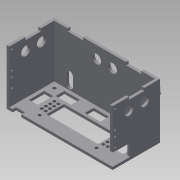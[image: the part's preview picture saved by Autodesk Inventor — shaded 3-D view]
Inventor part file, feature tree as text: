
AUTODESK INVENTOR PART (.ipt)
format: ipt  version: 2015 SP1 (Build 190203100, 203)  size: 1,242,624 bytes
history: native  units: mm
features: extrude x27, sketch x23, projected_geometry x7, fillet x1, plane x1, chamfer x1
ambient origin geometry x8: Origin, YZ Plane, XZ Plane, XY Plane, X Axis, Y Axis, Z Axis, Center Point
bodies: Body1 (feature_tree)
feature tree (60):
  sketch  "Sketch1"  dims[d49=120.812mm d51=3.0mm]
  extrude  "Extrusion5"  Depth=3.0mm
  extrude  "Extrusion6"  Depth=3.0mm TaperAngle=0.0deg
  extrude  "Extrusion7"  Depth=3.0mm
  extrude  "Extrusion8"  Depth=51.214111mm
  extrude  "Extrusion9"  Depth=3.5mm TaperAngle=0.0deg
  extrude  "Extrusion10"  Depth=17.5mm
  sketch  "Sketch12"  dims[d65=10.0mm d66=17.5mm]
  extrude  "Extrusion11"  Depth=10.0mm TaperAngle=0.0deg
  extrude  "Extrusion12"  Depth=3.0mm TaperAngle=0.0deg
  fillet  "Fillet2"  Radius=22.0mm
  extrude  "Extrusion13"  Depth=15.0mm
  plane  "Work Plane1"
  sketch  "Sketch20"  dims[d80=3.0mm d81=0.0mm d82=10.0mm d83=0.0mm d84=22.0mm]
  extrude  "Extrusion26"  Depth=200.0mm TaperAngle=0.0deg
  sketch  "Sketch25"  dims[d87=10.0mm d88=200.0mm d89=0.0mm]
  extrude  "Extrusion28"  Depth=2.0mm
  extrude  "Extrusion29"  Depth=3.5mm
  extrude  "Extrusion30"  Depth=3.5mm
  chamfer  "Chamfer1"  Distance=10.0mm
  extrude  "Extrusion31"  Depth=6.5mm
  extrude  "Extrusion32"  Depth=10.0mm TaperAngle=0.0deg
  extrude  "Extrusion33"  Depth=7.5mm
  extrude  "Extrusion34"  Depth=22.5mm
  extrude  "Extrusion35"  Depth=3.0mm
  extrude  "Extrusion36"  Depth=7.5mm
  extrude  "Extrusion37"  Depth=15.0mm TaperAngle=0.0deg
  sketch  "Sketch40"  dims[d167=180.0deg d168=7.5mm]
  extrude  "Extrusion38"  Depth=3.0mm
  extrude  "Extrusion39"  Depth=3.5mm
  extrude  "Extrusion40"  Depth=3.5mm
  extrude  "Extrusion41"  Depth=3.0mm
  extrude  "Extrusion42"  Depth=3.5mm
  extrude  "Extrusion43"  Depth=3.5mm
  extrude  "Extrusion44"  Depth=3.0mm
  sketch  "Sketch6"  dims[d52=3.0mm d53=0.0mm d54=60.0mm d55=0.0mm]
  sketch  "Sketch7"  dims[d57=3.0mm d58=3.0mm]
  sketch  "Sketch9"  dims[d59=114.812mm d61=51.214111mm]
  sketch  "Sketch10"  dims[d62=3.5mm d63=10.0mm d64=0.0mm]
  sketch  "Sketch13"  dims[d69=10.0mm d72=10.0mm d73=0.0mm]
  sketch  "Sketch24"  dims[d85=22.0mm d86=15.0mm]
  sketch  "Sketch26"  dims[d90=200.0mm d91=0.0mm d92=2.0mm]
  sketch  "Sketch27"  dims[d95=3.5mm d96=3.5mm]
  projected_geometry  "Projected Loop1"
  projected_geometry  "Projected Loop2"
  sketch  "Sketch30"  dims[d97=3.5mm d99=20.0mm]
  sketch  "Sketch34"  dims[d100=55.0mm]
  projected_geometry  "Projected Loop6"
  sketch  "Sketch35"  dims[d101=3.5mm d102=10.0mm d103=0.0mm]
  sketch  "Sketch38"  dims[d121=19.75mm d132=6.5mm]
  sketch  "Sketch39"  dims[d164=20.0mm d165=10.0mm d166=0.0mm]
  sketch  "Sketch41"  dims[d169=7.5mm d172=22.5mm]
  sketch  "Sketch42"  dims[d173=3.0mm d174=22.5mm]
  projected_geometry  "Projected Loop8"
  sketch  "Sketch43"  dims[d175=15.0mm d176=0.0mm d177=7.5mm]
  projected_geometry  "Projected Loop9"
  sketch  "Sketch44"  dims[d178=7.5mm d179=15.0mm d180=0.0mm]
  sketch  "Sketch45"  dims[d187=2.0mm d188=3.0mm d189=6.5mm d190=2.0mm d191=3.0mm d192=6.5mm d193=2.0mm d194=3.0mm d195=2.0mm d196=3.0mm d197=6.5mm d198=6.5mm d199=0.5mm d200=15.0mm d201=0.0mm d202=5.0mm d203=2.0mm d204=45.0deg d223=10.0mm d224=0.0mm d225=17.5mm d226=10.0mm d227=17.5mm d228=6.0mm d229=10.0mm d230=0.0mm d240=10.25mm d241=10.25mm d242=18.0mm d243=9.0mm d246=10.25mm d247=10.25mm d248=18.0mm d249=9.0mm d250=10.0mm d251=0.0mm d252=10.0mm d253=0.0mm d254=37.5mm d255=37.5mm d256=79.49mm d257=7.5mm d258=7.5mm d259=5.0mm d260=5.0mm d261=10.0mm d262=0.0mm d263=2.0mm d264=0.0mm d265=2.0mm d266=2.0mm d267=3.0mm d268=3.0mm d269=10.785mm d270=20.723mm d271=2.0mm d272=0.0mm d273=3.5mm d274=3.5mm d275=4.7355mm d276=0.2385mm d277=0.2385mm d278=4.77mm d279=3.5mm d280=3.5mm d281=0.2385mm d282=0.2385mm d283=4.77mm d284=2.9885mm d286=2.0mm d287=0.0mm d298=4.77mm d299=2.0mm d300=0.0mm d301=2.9885mm d302=2.0mm d303=0.0mm d304=2.0mm d305=0.0mm d306=2.0mm d307=0.0mm d308=2.0mm d309=0.0mm d310=2.0mm d311=0.0mm]
  projected_geometry  "Projected Loop10"
  projected_geometry  "Projected Loop11"
